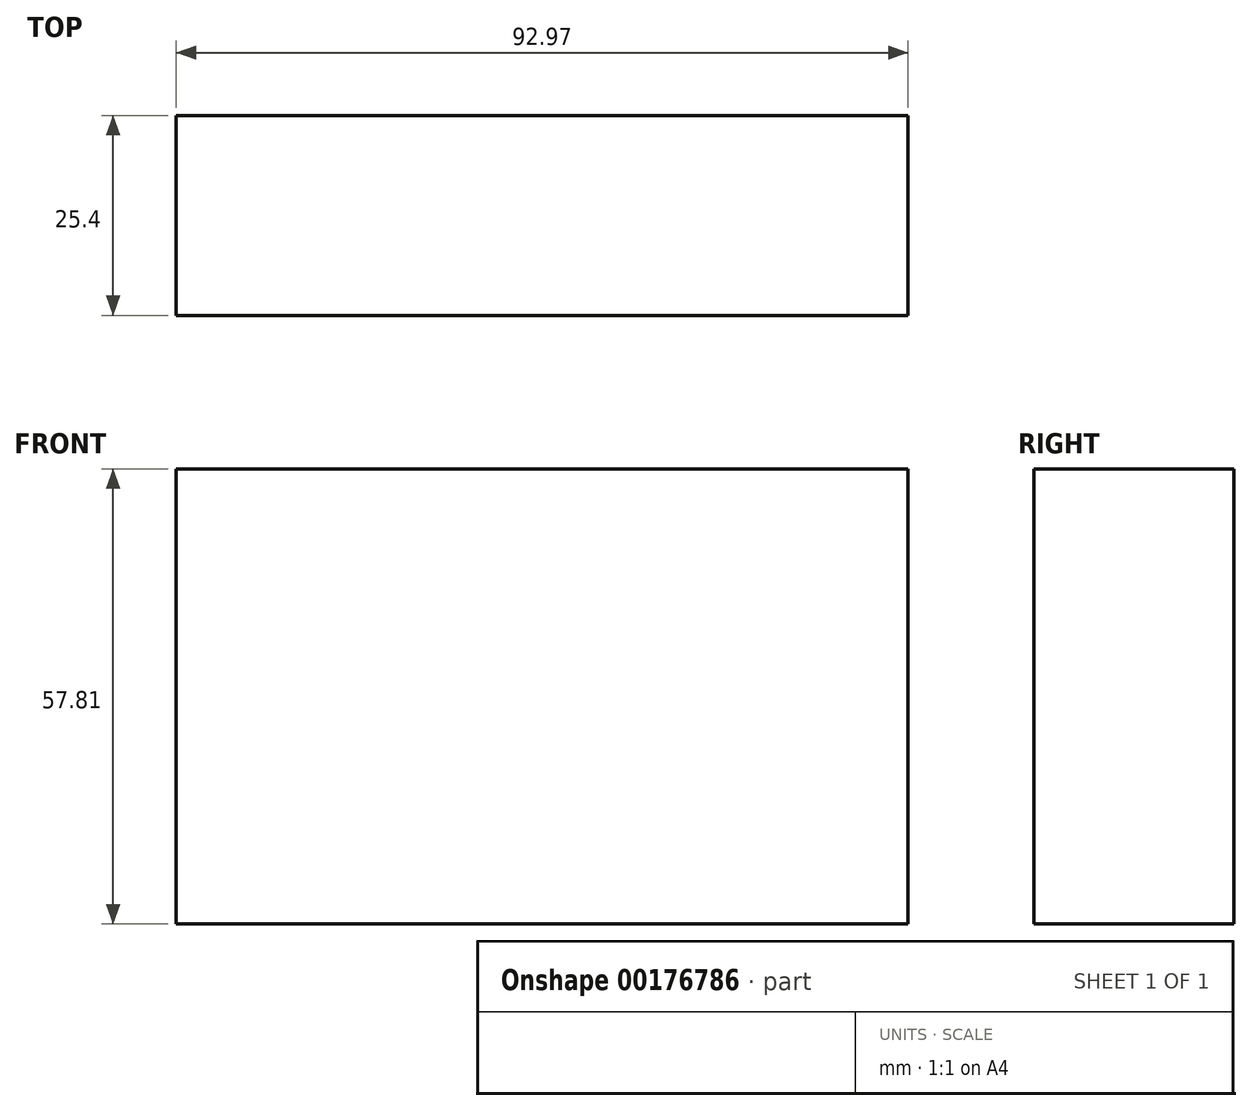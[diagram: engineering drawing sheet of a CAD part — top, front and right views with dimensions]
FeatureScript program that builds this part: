
annotation { "Feature Type Name" : "Feature", "Feature Type Description" : "" }
export const myFeature = defineFeature(function(context is Context, id is Id, definition is map)
    precondition{}
    {
        {
            var Q0;
            Q0=qCreatedBy(makeId("Front.planeOp"),FACE);
            var sketch = newSketch(context, id + "F0", { "sketchPlane" : qUnion([Q0])});
            skLineSegment(sketch, "E0.bottom", {"start": v(-56.62, -19.82) * mm, "end": v(36.35, -19.82) * mm});
            skLineSegment(sketch, "E0.top", {"start": v(-56.62, 38) * mm, "end": v(36.35, 38) * mm});
            skLineSegment(sketch, "E0.left", {"start": v(-56.62, -19.82) * mm, "end": v(-56.62, 38) * mm});
            skLineSegment(sketch, "E0.right", {"start": v(36.35, -19.82) * mm, "end": v(36.35, 38) * mm});
            skSolve(sketch);
        }
        {
            var Q0;
            Q0 = qSketchRegion(id + "F0", true);
            extrude(context, id + "F1", {"entities" : qUnion([Q0]), "depth" : 25.4 * mm});
        }
    });
